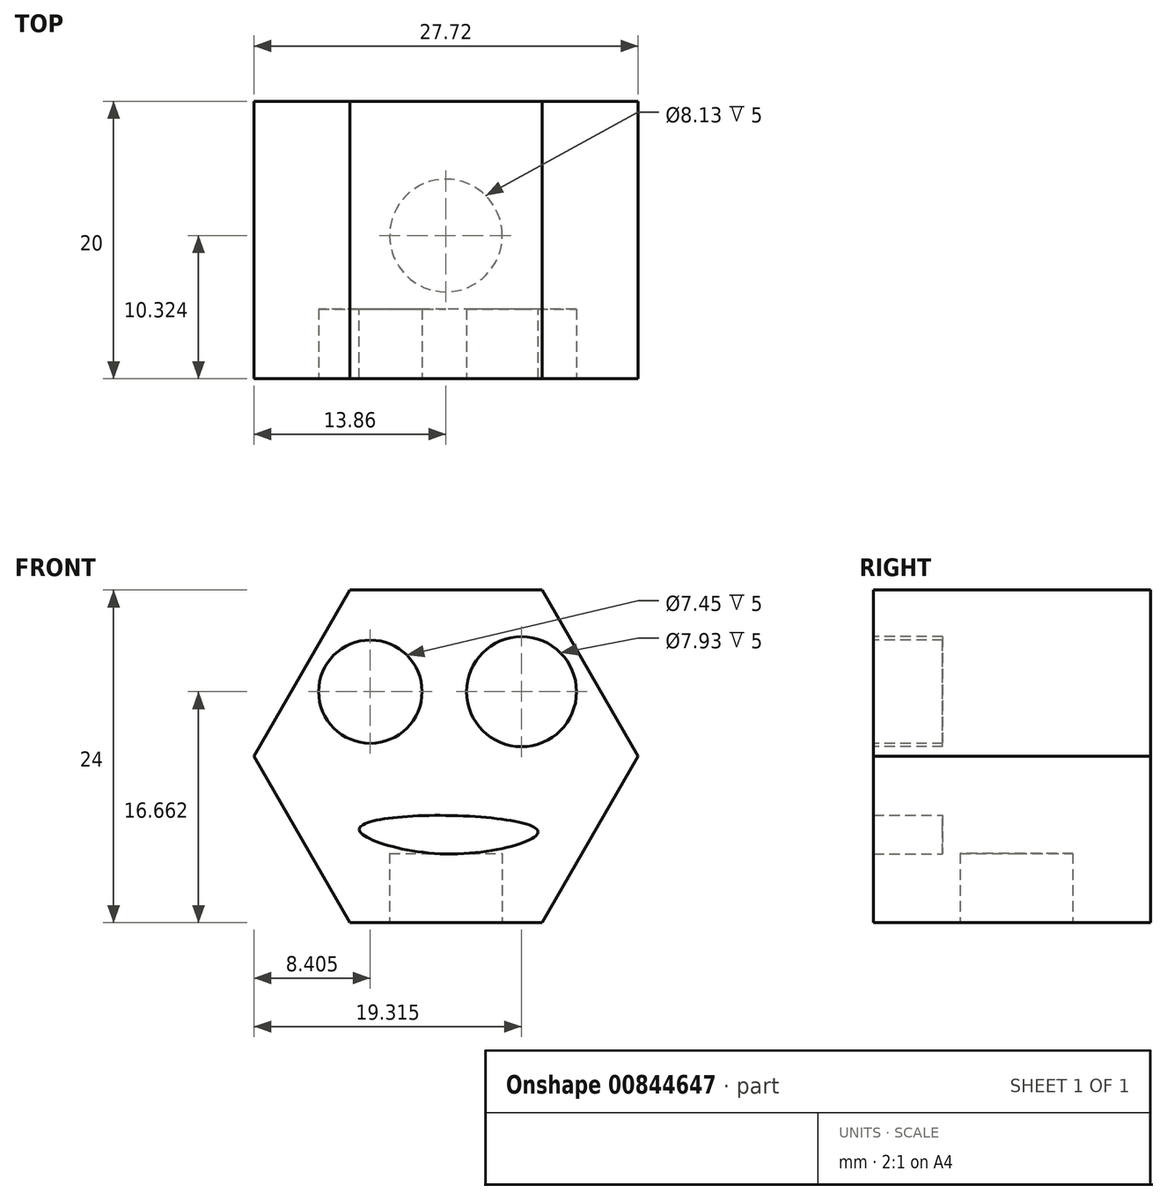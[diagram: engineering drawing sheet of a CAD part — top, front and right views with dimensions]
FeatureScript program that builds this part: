
annotation { "Feature Type Name" : "Feature", "Feature Type Description" : "" }
export const myFeature = defineFeature(function(context is Context, id is Id, definition is map)
    precondition{}
    {
        {
            var Q0;
            Q0=qCreatedBy(makeId("Front.planeOp"),FACE);
            var sketch = newSketch(context, id + "F0", { "sketchPlane" : qUnion([Q0])});
            skCircle(sketch, "E0.cCircle", {"center": v(0, 0) * mm, "radius": 12 * mm, "construction": true});
            skLineSegment(sketch, "E0.0", {"start": v(6.93, -12) * mm, "end": v(-6.93, -12) * mm});
            skLineSegment(sketch, "E0.1", {"start": v(-6.93, -12) * mm, "end": v(-13.86, 0) * mm});
            skLineSegment(sketch, "E0.2", {"start": v(-13.86, 0) * mm, "end": v(-6.93, 12) * mm});
            skLineSegment(sketch, "E0.3", {"start": v(-6.93, 12) * mm, "end": v(6.93, 12) * mm});
            skLineSegment(sketch, "E0.4", {"start": v(6.93, 12) * mm, "end": v(13.86, 0) * mm});
            skLineSegment(sketch, "E0.5", {"start": v(13.86, 0) * mm, "end": v(6.93, -12) * mm});
            skPoint(sketch, "E0.0.midPoint", {"position": v(0, -12) * mm});
            skSolve(sketch);
        }
        {
            var Q0;
            Q0=makeQuery(id+"F0.imprint","IMPRINT",FACE,{"disambiguationData":[TD([[makeQuery(id+"F0.imprint","IMPRINT",EDGE,{"derivedFrom":sQuery(id+"F0.wireOp",EDGE,"E0.0")}),-1.0]])]});
            extrude(context, id + "F1", {"entities" : qUnion([Q0]), "depth" : 20 * mm, "offsetDistance" : 25 * mm});
        }
        {
            var Q0;
            Q0=makeQuery(id+"F1.opExtrude","CAP_FACE",FACE,{"disambiguationData":[OSD([sQuery(id+"F0.wireOp",EDGE,"E0.0"),sQuery(id+"F0.wireOp",EDGE,"E0.1"),sQuery(id+"F0.wireOp",EDGE,"E0.2"),sQuery(id+"F0.wireOp",EDGE,"E0.3"),sQuery(id+"F0.wireOp",EDGE,"E0.4"),sQuery(id+"F0.wireOp",EDGE,"E0.5")])],"isStart":false});
            var sketch = newSketch(context, id + "F2", { "sketchPlane" : qUnion([Q0])});
            skCircle(sketch, "E1", {"center": v(-5.45, 4.66) * mm, "radius": 3.73 * mm});
            skCircle(sketch, "E2", {"center": v(5.45, 4.66) * mm, "radius": 3.97 * mm});
            skSolve(sketch);
        }
        {
            var Q0;
            Q0=makeQuery(id+"F2.imprint","IMPRINT",FACE,{"disambiguationData":[TD([[makeQuery(id+"F2.imprint","IMPRINT",EDGE,{"derivedFrom":sQuery(id+"F2.wireOp",EDGE,"E1")}),-1.0]])]});
            var sketch = newSketch(context, id + "F3", { "sketchPlane" : qUnion([Q0])});
            skFitSpline(sketch, "E3", {"points": [v(0, -7.04) * mm, v(-6.25, -5.26) * mm, v(0, -4.26) * mm, v(6.65, -5.45) * mm, v(0, -7.04) * mm]});
            skLineSegment(sketch, "E4", {"start": v(0, -4.26) * mm, "end": v(0, -7.04) * mm});
            skLineSegment(sketch, "E5", {"start": v(-6.25, -5.26) * mm, "end": v(6.65, -5.45) * mm});
            skSolve(sketch);
        }
        {
            var Q0;
            Q0=makeQuery(id+"F2.imprint","IMPRINT",FACE,{"disambiguationData":[TD([[makeQuery(id+"F2.imprint","IMPRINT",EDGE,{"derivedFrom":sQuery(id+"F2.wireOp",EDGE,"E2")}),1.0]])]});
            var Q1;
            Q1=makeQuery(id+"F2.imprint","IMPRINT",FACE,{"disambiguationData":[TD([[makeQuery(id+"F2.imprint","IMPRINT",EDGE,{"derivedFrom":sQuery(id+"F2.wireOp",EDGE,"E1")}),1.0]])]});
            extrude(context, id + "F4", {"entities" : qUnion([Q0, Q1]), "operationType" : NewBodyOperationType.REMOVE, "oppositeDirection" : true, "depth" : 5 * mm, "offsetDistance" : 25 * mm});
        }
        {
            var Q0;
            Q0=sQuery(id+"F3.wireOp",EDGE,"E3");
            extrude(context, id + "F5", {"bodyType" : ToolBodyType.SURFACE, "surfaceEntities" : qUnion([Q0]), "depth" : -5 * mm, "offsetDistance" : 25 * mm});
        }
        {
            var Q0;
            Q0=makeQuery(id+"F1.opExtrude","SWEPT_FACE",FACE,{"disambiguationData":[OSD([sQuery(id+"F0.wireOp",EDGE,"E0.0")])]});
            var sketch = newSketch(context, id + "F6", { "sketchPlane" : qUnion([Q0])});
            skCircle(sketch, "E6", {"center": v(0, 9.68) * mm, "radius": 4.06 * mm});
            skSolve(sketch);
        }
        {
            var Q0;
            Q0=makeQuery(id+"F6.imprint","IMPRINT",FACE,{"disambiguationData":[TD([[makeQuery(id+"F6.imprint","IMPRINT",EDGE,{"derivedFrom":sQuery(id+"F6.wireOp",EDGE,"E6")}),1.0]])]});
            extrude(context, id + "F7", {"entities" : qUnion([Q0]), "operationType" : NewBodyOperationType.REMOVE, "oppositeDirection" : true, "depth" : 5 * mm, "offsetDistance" : 25 * mm});
        }
        {
            var Q0;
            {var subQ0=sQuery(id+"F3.wireOp",EDGE,"E4");var subQ1=sQuery(id+"F3.wireOp",EDGE,"E3");var subQ2=makeQuery(id+"F3.imprint","INTERSECT",VERTEX,{"disambiguationData":[OD(0.0)],"derivedFrom":[subQ1,subQ0]});Q0=makeQuery(id+"F3.imprint","IMPRINT",FACE,{"disambiguationData":[TD([[makeQuery(id+"F3.imprint","IMPRINT",EDGE,{"disambiguationData":[TD([[subQ2,1.0]])],"derivedFrom":subQ1}),-1.0]])]});}
            var Q1;
            {var subQ0=sQuery(id+"F3.wireOp",EDGE,"E4");var subQ1=sQuery(id+"F3.wireOp",EDGE,"E3");var subQ2=makeQuery(id+"F3.imprint","INTERSECT",VERTEX,{"disambiguationData":[OD(1.0)],"derivedFrom":[subQ1,subQ0]});Q1=makeQuery(id+"F3.imprint","IMPRINT",FACE,{"disambiguationData":[TD([[makeQuery(id+"F3.imprint","IMPRINT",EDGE,{"disambiguationData":[TD([[subQ2,-1.0]])],"derivedFrom":subQ1}),-1.0]])]});}
            var Q2;
            {var subQ0=sQuery(id+"F3.wireOp",EDGE,"E4");var subQ1=sQuery(id+"F3.wireOp",EDGE,"E3");var subQ2=makeQuery(id+"F3.imprint","INTERSECT",VERTEX,{"disambiguationData":[OD(1.0)],"derivedFrom":[subQ1,subQ0]});Q2=makeQuery(id+"F3.imprint","IMPRINT",FACE,{"disambiguationData":[TD([[makeQuery(id+"F3.imprint","IMPRINT",EDGE,{"disambiguationData":[TD([[subQ2,1.0]])],"derivedFrom":subQ1}),-1.0]])]});}
            var Q3;
            {var subQ0=sQuery(id+"F3.wireOp",EDGE,"E4");var subQ1=sQuery(id+"F3.wireOp",EDGE,"E3");var subQ2=makeQuery(id+"F3.imprint","INTERSECT",VERTEX,{"disambiguationData":[OD(0.0)],"derivedFrom":[subQ1,subQ0]});Q3=makeQuery(id+"F3.imprint","IMPRINT",FACE,{"disambiguationData":[TD([[makeQuery(id+"F3.imprint","IMPRINT",EDGE,{"disambiguationData":[TD([[subQ2,-1.0]])],"derivedFrom":subQ1}),-1.0]])]});}
            extrude(context, id + "F8", {"entities" : qUnion([Q0, Q1, Q2, Q3]), "operationType" : NewBodyOperationType.REMOVE, "oppositeDirection" : true, "depth" : 5 * mm, "offsetDistance" : 25 * mm});
        }
    });
